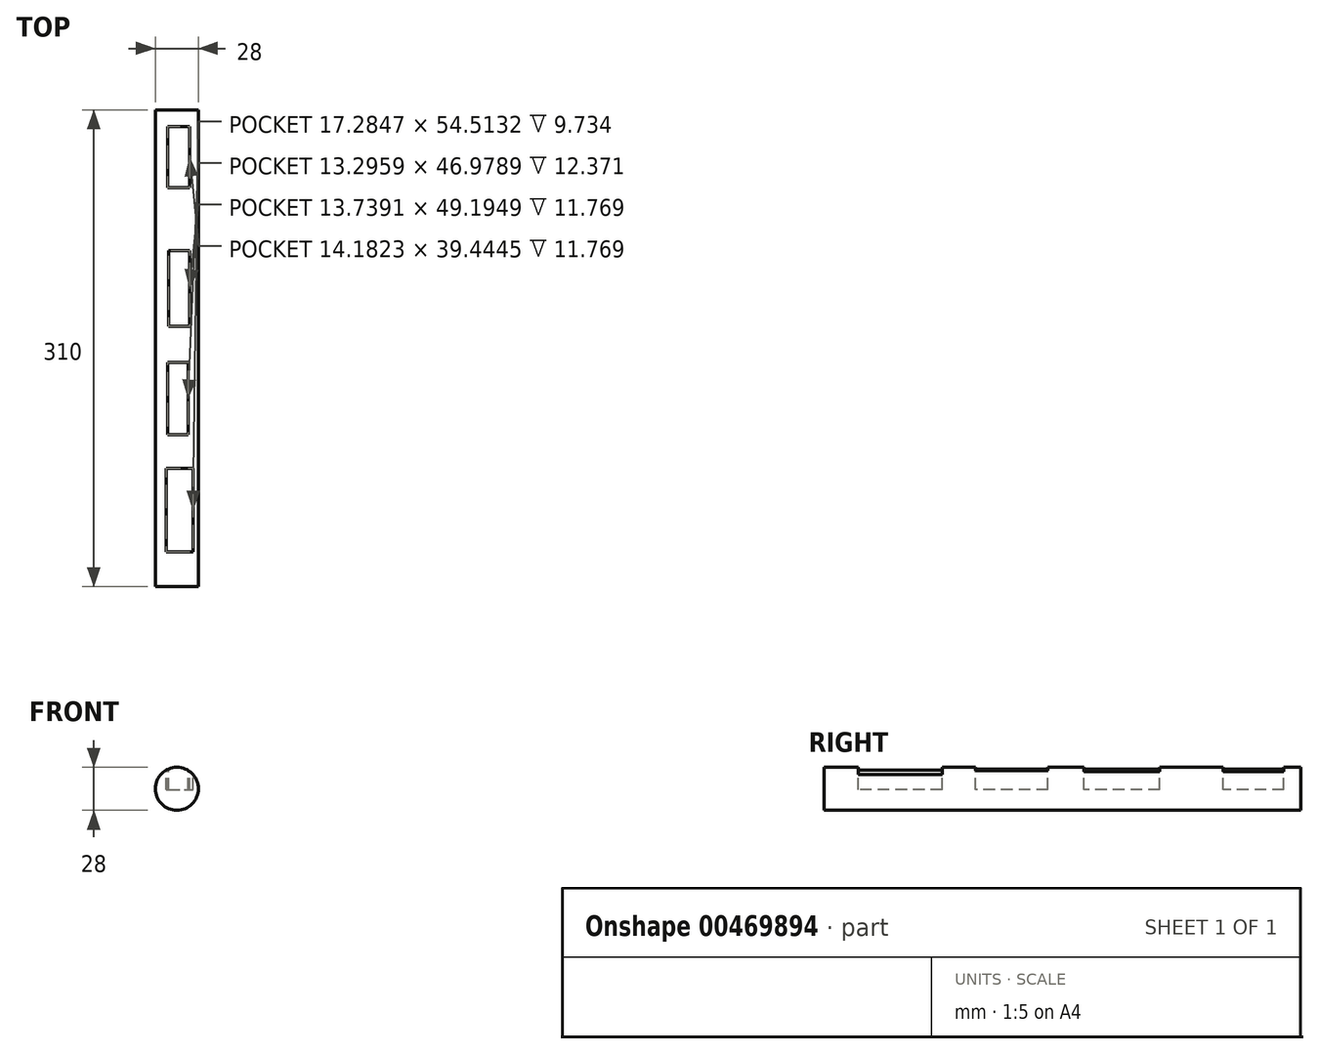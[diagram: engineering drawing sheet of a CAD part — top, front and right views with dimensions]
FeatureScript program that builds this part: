
annotation { "Feature Type Name" : "Feature", "Feature Type Description" : "" }
export const myFeature = defineFeature(function(context is Context, id is Id, definition is map)
    precondition{}
    {
        {
            var Q0;
            Q0=qCreatedBy(makeId("Front.planeOp"),FACE);
            var sketch = newSketch(context, id + "F0", { "sketchPlane" : qUnion([Q0])});
            skCircle(sketch, "E0", {"center": v(0, 0) * mm, "radius": 14 * mm});
            skSolve(sketch);
        }
        {
            var Q0;
            Q0 = qSketchRegion(id + "F0", true);
            extrude(context, id + "F1", {"entities" : qUnion([Q0]), "depth" : 310 * mm});
        }
        {
            var Q0;
            Q0=qCreatedBy(makeId("Top.planeOp"),FACE);
            cPlane(context, id + "F2", {"entities" : qUnion([Q0]), "cplaneType" : CPlaneType.OFFSET, "offset" : (29 / 2) * mm, "width" : 150 * mm, "height" : 150 * mm});
        }
        {
            var Q0;
            Q0=qCreatedBy(id+"F2.planeOp",FACE);
            var sketch = newSketch(context, id + "F3", { "sketchPlane" : qUnion([Q0])});
            skLineSegment(sketch, "E1.bottom", {"start": v(-5.87, -11.02) * mm, "end": v(8.3, -11.02) * mm});
            skLineSegment(sketch, "E1.top", {"start": v(-5.87, -50.47) * mm, "end": v(8.3, -50.47) * mm});
            skLineSegment(sketch, "E1.left", {"start": v(-5.87, -11.02) * mm, "end": v(-5.87, -50.47) * mm});
            skLineSegment(sketch, "E1.right", {"start": v(8.3, -11.02) * mm, "end": v(8.3, -50.47) * mm});
            skLineSegment(sketch, "E2.bottom", {"start": v(-5.43, -91.69) * mm, "end": v(8.3, -91.69) * mm});
            skLineSegment(sketch, "E2.top", {"start": v(-5.43, -140.88) * mm, "end": v(8.3, -140.88) * mm});
            skLineSegment(sketch, "E2.left", {"start": v(-5.43, -91.69) * mm, "end": v(-5.43, -140.88) * mm});
            skLineSegment(sketch, "E2.right", {"start": v(8.3, -91.69) * mm, "end": v(8.3, -140.88) * mm});
            skLineSegment(sketch, "E3.bottom", {"start": v(-5.87, -164.37) * mm, "end": v(7.42, -164.37) * mm});
            skLineSegment(sketch, "E3.top", {"start": v(-5.87, -211.35) * mm, "end": v(7.42, -211.35) * mm});
            skLineSegment(sketch, "E3.left", {"start": v(-5.87, -164.37) * mm, "end": v(-5.87, -211.35) * mm});
            skLineSegment(sketch, "E3.right", {"start": v(7.42, -164.37) * mm, "end": v(7.42, -211.35) * mm});
            skLineSegment(sketch, "E4.bottom", {"start": v(-6.76, -233.07) * mm, "end": v(10.52, -233.07) * mm});
            skLineSegment(sketch, "E4.top", {"start": v(-6.76, -287.58) * mm, "end": v(10.52, -287.58) * mm});
            skLineSegment(sketch, "E4.left", {"start": v(-6.76, -233.07) * mm, "end": v(-6.76, -287.58) * mm});
            skLineSegment(sketch, "E4.right", {"start": v(10.52, -233.07) * mm, "end": v(10.52, -287.58) * mm});
            skSolve(sketch);
        }
        {
            var Q0;
            Q0 = qSketchRegion(id + "F3", true);
            extrude(context, id + "F4", {"entities" : qUnion([Q0]), "operationType" : NewBodyOperationType.REMOVE, "oppositeDirection" : true, "depth" : 15 * mm});
        }
    });
